# Revit family: Tub_Faucet_Handshower-Grohe-Tempesta-25277_Series
name_source: partatom
category: Plumbing Fixtures
units: mm (PartAtom-declared; Revit-internal decimal feet)

## family parameters
Always vertical = No
Cut with Voids When Loaded = No
OmniClass Number = 23.45.55.14
OmniClass Title = Single Faucets
Part Type = Normal
Room Calculation Point = No
Round Connector Dimension = Use Diameter
Shared = Yes
Work Plane-Based = Yes

## types (2) — shared parameters
(26 047) Tempesta Round 110 Hand Shower = Yes
Aerator Reach = 4 5/16"
Assembly Code = D2020300
CW Connection = Yes
CWFU = 3
Compliance Certifications = • CEC Certified • CALGreen Compliant • Massachusetts Plumbing Board Approved • Energy Policy Act of 1992 • CSA B125.1 • ASME A112.18.1
Default Elevation = 0"
Description = 4-HOLE SINGLE HANDLE DECK MOUNT ROMAN TUB FAUCET WITH 1.5 GPM HAND SHOWER
Flow Rate = 1.5gpm (5.7L/min)
HW Connection = Yes
HWFU = 3
Height = 9 15/16"
Installation Type = Deck Mounted
Length = 19 3/4"
Manufacturer = Grohe
Spout Reach = 6 13/32"
Tempered Water Connection Diameter = 1/2"
URL = https://www.grohe.com
Vent Connection = No
WFU = 4
Waste Connection = No

## per-type parameters (varying)
| type | Finish | Material |
| 25277003 | Metal-Grohe-003-StarLight Chrome | Metal-Grohe-003-StarLight Chrome |
| 25277EN3 | Metal-Grohe-EN3-Brushed Nickel Infinity Finish | Metal-Grohe-EN3-Brushed Nickel Infinity Finish |

note: column(s) folded — value = type name in every type: Model

## geometry (parser evidence)
native form markers: Sweep x5
no freeform markers — native parametric forms only
